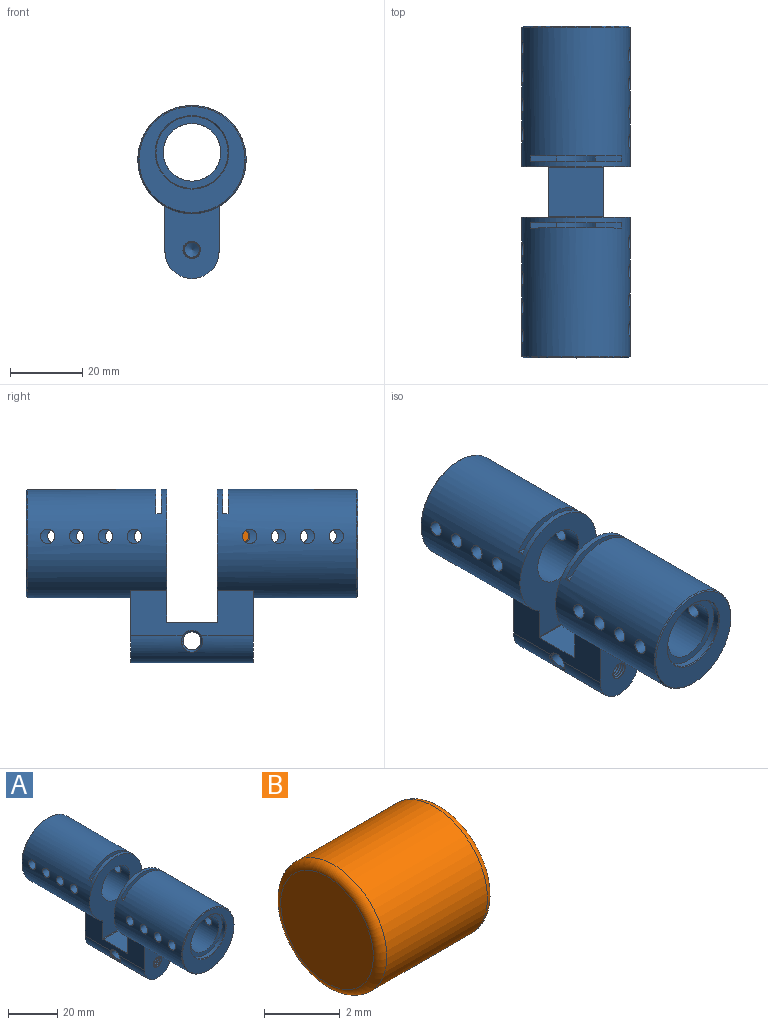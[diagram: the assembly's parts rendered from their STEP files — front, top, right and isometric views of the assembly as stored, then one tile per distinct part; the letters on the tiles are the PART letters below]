
ASSEMBLY  parts=2 mates=1
PART A: 69 faces, bbox 30.1x92.1x48.1 mm
  f0: plane 34x12.5mm, normal (-1,0,0), area 294.1mm2, adj f1,f2,f3,f6,f7,f9,f34,f35
  f1: cylinder r=7.5mm len=34mm, axis (0,-1,0), area 752.9mm2, adj f0,f4,f6,f37,f65,f67
  f2: cylinder r=15mm len=38.7mm, axis (0,1,0), area 3344mm2, adj f0,f3,f4,f6,f8,f10,f11,f12
  f3: plane 36.79x30mm, normal (0,-1,0), area 617.4mm2, adj f0,f2,f4,f9,f20
  f4: plane 34x12.5mm, normal (1,0,0), area 294.1mm2, adj f1,f2,f3,f6,f7,f9,f34,f35
  f5: plane 29.4x29.4mm, normal (0,1,0), area 352mm2, adj f8,f21
  f6: plane 20.1x15.1mm, normal (0,1,0), area 238.2mm2, adj f0,f1,f2,f4,f24,f31,f32
  f7: plane 15x13.6mm, normal (0,0,1), area 204mm2, adj f0,f4,f9,f39
  f8: cone r=15mm half-angle=45deg, axis (0,-1,0), area 39.6mm2, adj f2,f5
  f9: cylinder r=0.2mm len=15mm, axis (-1,0,0), area 4.7mm2, adj f0,f3,f4,f7
  f10: cylinder r=2mm len=7.25mm, axis (1,0,0), area 91.2mm2, adj f2,f20
  f11: cylinder r=2mm len=7.25mm, axis (1,0,0), area 91.2mm2, adj f2,f20
  f12: cylinder r=2mm len=7.25mm, axis (1,0,0), area 91.2mm2, adj f2,f20
  f13: cylinder r=2mm len=7.25mm, axis (1,0,0), area 91.2mm2, adj f2,f20
  f14: cylinder r=2mm len=6.71mm, axis (-1,0,0), area 84.3mm2, adj f2,f20
  f15: cylinder r=2mm len=6.71mm, axis (-1,0,0), area 84.3mm2, adj f2,f20
  f16: cylinder r=2mm len=6.71mm, axis (-1,0,0), area 84.3mm2, adj f2,f20
  f17: cylinder r=2mm len=6.71mm, axis (-1,0,0), area 84.3mm2, adj f2,f20
  f18: cylinder r=10mm len=20mm, axis (0,1,0), area 113.1mm2, adj f19,f21
  f19: plane 20x20mm, normal (0,1,0), area 113.1mm2, adj f18,f20
  f20: cylinder r=8mm len=37mm, axis (0,1,0), area 1741.3mm2, adj f3,f10,f11,f12,f13,f14,f15,f16
  f21: cone r=10mm half-angle=45deg, axis (0,1,0), area 17.9mm2, adj f5,f18
  f22: cone r=0mm half-angle=59deg, axis (0,1,0), area 16.2mm2, adj f23
  f23: cylinder r=2.1mm len=9.8mm, axis (0,1,0), area -2.2mm2, adj f22,f24,f31,f32,f33
  f24: cone r=2.1mm half-angle=45deg, axis (0,1,0), area 1.2mm2, adj f6,f23,f31,f32
  f25: plane 1.5x0.29mm, normal (1,0,0), area 0.4mm2, adj f2,f27,f28,f30
  f26: plane 1.5x0.29mm, normal (-1,0,0), area 0.4mm2, adj f2,f27,f29,f30
  f27: plane 25x7mm, normal (0,1,0), area 110.8mm2, adj f2,f20,f25,f26,f28,f29
  f28: plane 7.21x1.5mm, normal (0,0,1), area 10.8mm2, adj f20,f25,f27,f30
  f29: plane 7.21x1.5mm, normal (0,0,1), area 10.8mm2, adj f20,f26,f27,f30
  f30: plane 25x7mm, normal (0,-1,0), area 110.8mm2, adj f2,f20,f25,f26,f28,f29
  f31: bspline ~10.11x5.77mm, area 93.3mm2, adj f6,f23,f24,f32,f33
  f32: bspline ~10.24x5.77mm, area 99.2mm2, adj f6,f23,f24,f31,f33
  f33: plane 0.75x0.4mm, normal (0,0,1), area 0.1mm2, adj f23,f31,f32
  f34: cylinder r=15mm len=38.7mm, axis (0,-1,0), area 3344.4mm2, adj f0,f4,f35,f37,f38,f40,f41,f42
  f35: plane 36.79x30mm, normal (0,1,0), area 617.4mm2, adj f0,f4,f34,f39,f50
  f36: plane 29.4x29.4mm, normal (0,-1,0), area 352mm2, adj f38,f51
  f37: plane 20.1x15.1mm, normal (0,-1,0), area 238.2mm2, adj f0,f1,f4,f34,f54,f61,f62
  f38: cone r=15mm half-angle=45deg, axis (0,1,0), area 39.6mm2, adj f34,f36
  f39: cylinder r=0.2mm len=15mm, axis (-1,0,0), area 4.7mm2, adj f0,f4,f7,f35
  f40: cylinder r=2mm len=7.25mm, axis (1,0,0), area 91.2mm2, adj f34,f50
  f41: cylinder r=2mm len=7.25mm, axis (1,0,0), area 91.2mm2, adj f34,f50
  f42: cylinder r=2mm len=7.25mm, axis (1,0,0), area 91.2mm2, adj f34,f50
  f43: cylinder r=2mm len=7.25mm, axis (1,0,0), area 91.2mm2, adj f34,f50
  f44: cylinder r=2mm len=6.71mm, axis (-1,0,0), area 84.3mm2, adj f34,f50
  f45: cylinder r=2mm len=6.71mm, axis (-1,0,0), area 84.3mm2, adj f34,f50
  f46: cylinder r=2mm len=6.71mm, axis (-1,0,0), area 84.3mm2, adj f34,f50
  f47: cylinder r=2mm len=6.71mm, axis (-1,0,0), area 84.3mm2, adj f34,f50
  f48: cylinder r=10mm len=20mm, axis (0,-1,0), area 113.1mm2, adj f49,f51
  f49: plane 20x20mm, normal (0,-1,0), area 113.1mm2, adj f48,f50
  f50: cylinder r=8mm len=37mm, axis (0,-1,0), area 1740.9mm2, adj f35,f40,f41,f42,f43,f44,f45,f46
  f51: cone r=10mm half-angle=45deg, axis (0,-1,0), area 17.9mm2, adj f36,f48
  f52: cone r=0mm half-angle=59deg, axis (0,-1,0), area 16.2mm2, adj f53
  f53: cylinder r=2.1mm len=9.8mm, axis (0,-1,0), area 17.7mm2, adj f52,f54,f61,f62,f63
  f54: cone r=2.1mm half-angle=45deg, axis (0,-1,0), area 1.2mm2, adj f37,f53,f61,f62
  f55: plane 1.5x0.29mm, normal (1,0,0), area 0.4mm2, adj f34,f57,f58,f60
  f56: plane 1.5x0.29mm, normal (-1,0,0), area 0.4mm2, adj f34,f57,f59,f60
  f57: plane 25x7mm, normal (0,-1,0), area 110.8mm2, adj f34,f50,f55,f56,f58,f59
  f58: plane 7.21x1.5mm, normal (0,0,1), area 10.8mm2, adj f50,f55,f57,f60
  f59: plane 7.21x1.5mm, normal (0,0,1), area 10.8mm2, adj f50,f56,f57,f60
  f60: plane 25x7mm, normal (0,1,0), area 110.8mm2, adj f34,f50,f55,f56,f58,f59
  f61: bspline ~10.11x5.77mm, area 93.3mm2, adj f37,f53,f54,f62,f63
  f62: bspline ~10.24x5.77mm, area 96.7mm2, adj f37,f53,f54,f61,f63
  f63: plane 0.75x0.4mm, normal (0,0,1), area 0.1mm2, adj f53,f61,f62
  f64: cylinder r=2.5mm len=14.2mm, axis (-1,0,0), area 223.1mm2, adj f65,f66,f67,f68
  f65: bspline ~5.8x4.65mm, area 7.6mm2, adj f1,f64,f66
  f66: cone r=2.5mm half-angle=45deg, axis (-1,0,0), area 3.1mm2, adj f0,f64,f65
  f67: bspline ~5.8x4.65mm, area 7.6mm2, adj f1,f64,f68
  f68: cone r=2.5mm half-angle=45deg, axis (1,0,0), area 3.1mm2, adj f4,f64,f67
PART B: 7 faces, bbox 4.2x4.3x4.3 mm
  f0: plane 3.45x3.45mm, normal (-1,0,0), area 9.3mm2, adj f6
  f1: plane 2.5x2.5mm, normal (1,0,0), area 4.9mm2, adj f5
  f2: cylinder r=1.5mm len=3.25mm, axis (-1,0,0), area 30.6mm2, adj f3,f5
  f3: torus R=1.74mm, axis (-1,0,0), area 8.1mm2, adj f2,f4
  f4: cylinder r=1.98mm len=3.95mm, axis (-1,0,0), area 46.5mm2, adj f3,f6
  f5: torus R=1.25mm, axis (1,0,0), area 3.5mm2, adj f1,f2
  f6: torus R=1.72mm, axis (-1,0,0), area 4.6mm2, adj f0,f4
PLACE A t=(-19.62,2.06,-10.66)mm fixed
PLACE B t=(-6.97,-38.44,-8.66)mm
MATE slider B.f2 <-> A.f43  axis (-1,0,0) through (-5.97,-38.44,-8.66)mm
